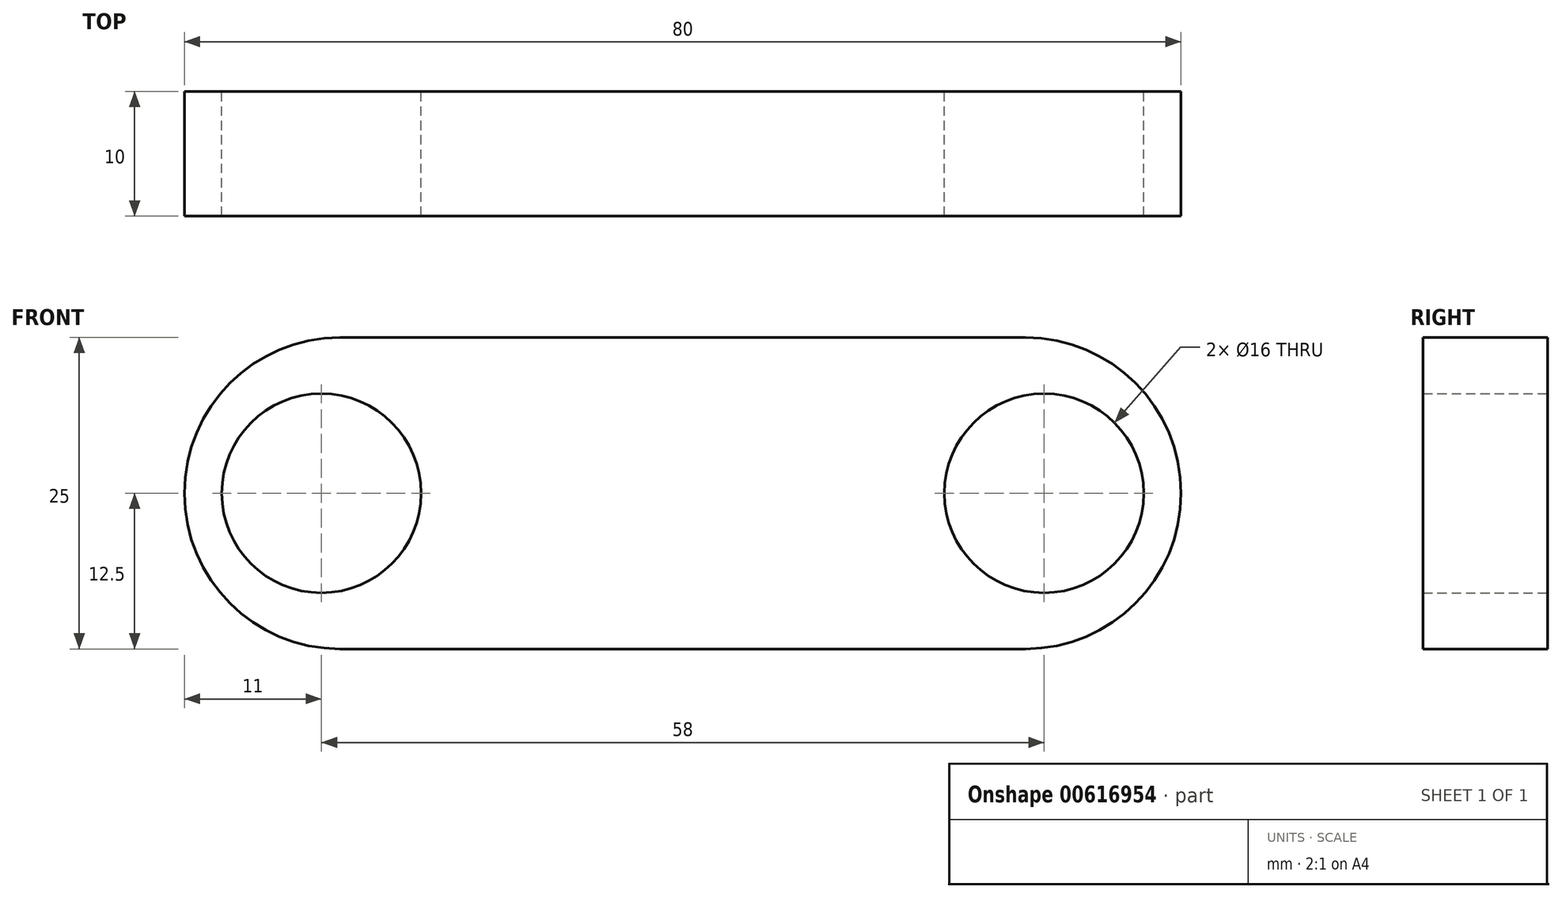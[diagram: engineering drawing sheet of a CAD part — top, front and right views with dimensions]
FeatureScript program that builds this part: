
annotation { "Feature Type Name" : "Feature", "Feature Type Description" : "" }
export const myFeature = defineFeature(function(context is Context, id is Id, definition is map)
    precondition{}
    {
        {
            var Q0;
            Q0=qCreatedBy(makeId("Front.planeOp"),FACE);
            var sketch = newSketch(context, id + "F0", { "sketchPlane" : qUnion([Q0])});
            skLineSegment(sketch, "E0.bottom", {"start": v(27.5, -12.5) * mm, "end": v(-27.5, -12.5) * mm});
            skLineSegment(sketch, "E0.top", {"start": v(27.5, 12.5) * mm, "end": v(-27.5, 12.5) * mm});
            skLineSegment(sketch, "E0.left", {"start": v(40, 0) * mm, "end": v(40, 0) * mm});
            skLineSegment(sketch, "E0.right", {"start": v(-40, 0) * mm, "end": v(-40, 0) * mm});
            skPoint(sketch, "E0.middle", {"position": v(0, 0) * mm});
            skLineSegment(sketch, "E1", {"start": v(-29, 12.5) * mm, "end": v(-29, -12.5) * mm});
            skLineSegment(sketch, "E2", {"start": v(29, 12.5) * mm, "end": v(29, -12.5) * mm});
            skCircle(sketch, "E3", {"center": v(-29, 0) * mm, "radius": 8 * mm});
            skCircle(sketch, "E4", {"center": v(29, 0) * mm, "radius": 8 * mm});
            skPoint(sketch, "E5.visualSharp", {"position": v(-40, 12.5) * mm});
            skArc(sketch, "E5.filletArc", {"start": v(-27.5, 12.5) * mm, "mid": v(-36.34, 8.84) * mm, "end": v(-40, 0) * mm});
            skPoint(sketch, "E6.visualSharp", {"position": v(-40, -12.5) * mm});
            skArc(sketch, "E6.filletArc", {"start": v(-40, 0) * mm, "mid": v(-36.34, -8.84) * mm, "end": v(-27.5, -12.5) * mm});
            skPoint(sketch, "E7.visualSharp", {"position": v(40, -12.5) * mm});
            skArc(sketch, "E7.filletArc", {"start": v(27.5, -12.5) * mm, "mid": v(36.34, -8.84) * mm, "end": v(40, 0) * mm});
            skPoint(sketch, "E8.visualSharp", {"position": v(40, 12.5) * mm});
            skArc(sketch, "E8.filletArc", {"start": v(40, 0) * mm, "mid": v(36.34, 8.84) * mm, "end": v(27.5, 12.5) * mm});
            skSolve(sketch);
        }
        {
            var Q0;
            Q0 = qSketchRegion(id + "F0", true);
            extrude(context, id + "F1", {"entities" : qUnion([Q0]), "depth" : 10 * mm, "offsetDistance" : 25 * mm});
        }
    });
